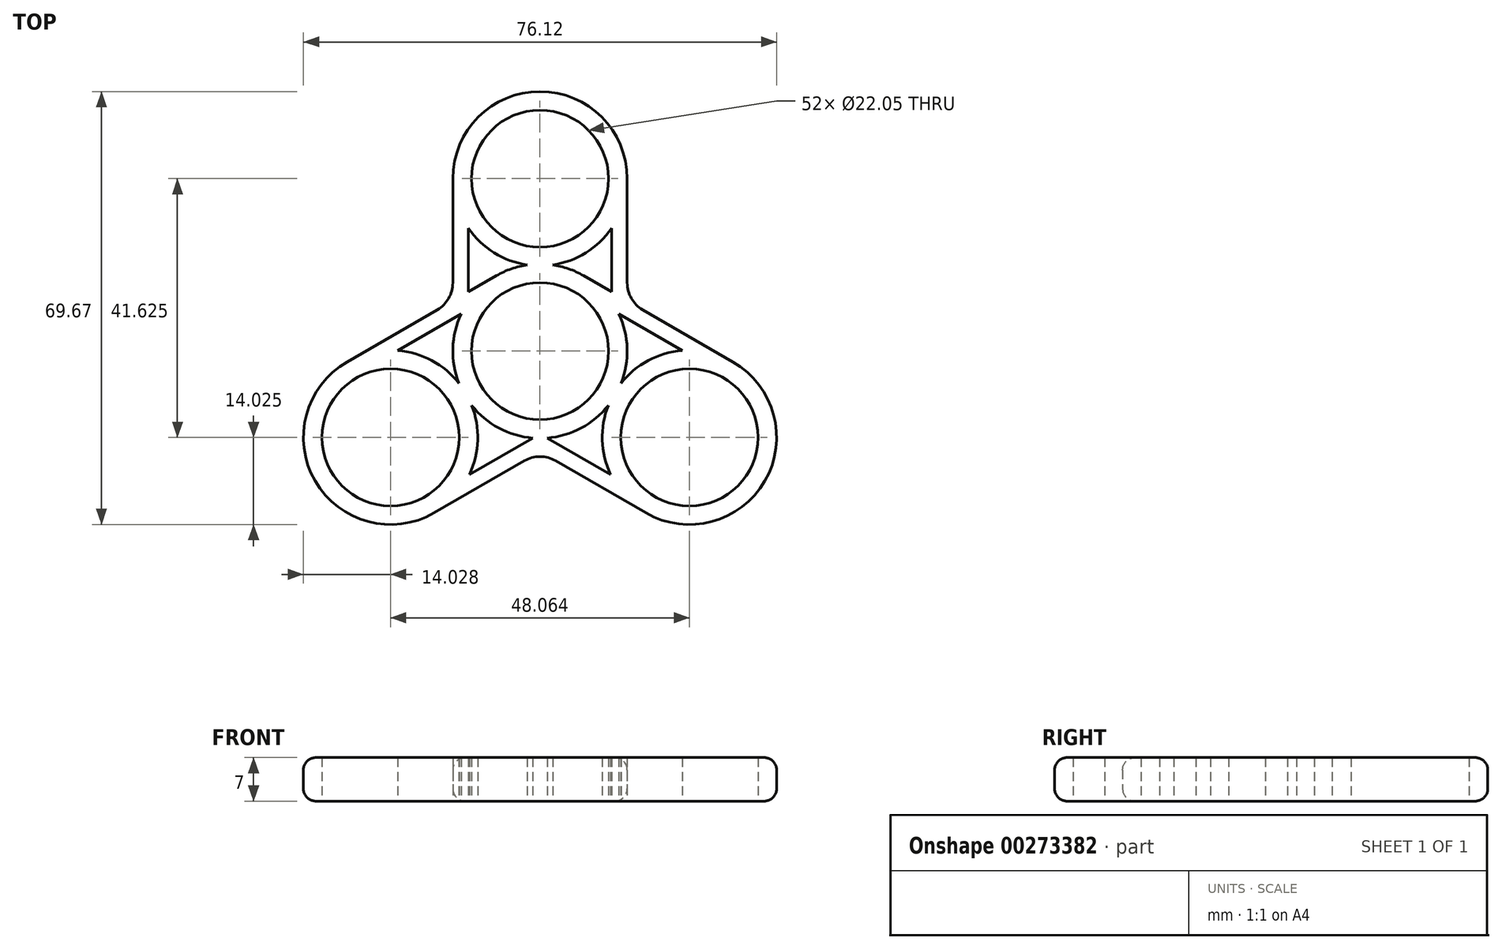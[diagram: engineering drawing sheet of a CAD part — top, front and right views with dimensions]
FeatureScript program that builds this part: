
annotation { "Feature Type Name" : "Feature", "Feature Type Description" : "" }
export const myFeature = defineFeature(function(context is Context, id is Id, definition is map)
    precondition{}
    {
        {
            var Q0;
            Q0=qCreatedBy(makeId("Top.planeOp"),FACE);
            var sketch = newSketch(context, id + "F0", { "sketchPlane" : qUnion([Q0])});
            skCircle(sketch, "E0", {"center": v(0, 0) * mm, "radius": 11.03 * mm});
            skCircle(sketch, "E1", {"center": v(0, 27.75) * mm, "radius": 11.03 * mm});
            skArc(sketch, "E2", {"start": v(2.05, 13.88) * mm, "mid": v(7.4, 15.83) * mm, "end": v(11.52, 19.76) * mm});
            skArc(sketch, "E3", {"start": v(-2.05, 13.88) * mm, "mid": v(-4.61, 13.25) * mm, "end": v(-7.01, 12.15) * mm});
            skLineSegment(sketch, "E4", {"start": v(-14.02, 27.75) * mm, "end": v(-14.02, 10.98) * mm});
            skLineSegment(sketch, "E5", {"start": v(-11.52, 9.54) * mm, "end": v(-11.52, 19.76) * mm});
            skArc(sketch, "E6.trimOffspring", {"start": v(-11.52, 19.76) * mm, "mid": v(-7.4, 15.83) * mm, "end": v(-2.05, 13.88) * mm});
            skLineSegment(sketch, "E7.MirrorCS", {"start": v(11.52, 9.54) * mm, "end": v(11.52, 19.76) * mm});
            skLineSegment(sketch, "E8.MirrorCS", {"start": v(14.02, 27.75) * mm, "end": v(14.02, 10.98) * mm});
            skArc(sketch, "E9.trimOffspring", {"start": v(14.02, 27.75) * mm, "mid": v(0, 41.77) * mm, "end": v(-14.02, 27.75) * mm});
            skArc(sketch, "E10.1.0", {"start": v(-11.35, -19.86) * mm, "mid": v(-10.01, -14.32) * mm, "end": v(-11, -8.7) * mm});
            skArc(sketch, "E10.1.1", {"start": v(-31.04, -1.73) * mm, "mid": v(-36.18, -20.89) * mm, "end": v(-17.02, -26.02) * mm});
            skArc(sketch, "E10.1.2", {"start": v(-13.04, -5.17) * mm, "mid": v(-17.4, -1.51) * mm, "end": v(-22.87, 0.1) * mm});
            skCircle(sketch, "E10.1.3", {"center": v(-24.03, -13.87) * mm, "radius": 11.03 * mm});
            skLineSegment(sketch, "E10.1.4", {"start": v(-12.68, 5.98) * mm, "end": v(-22.87, 0.1) * mm});
            skLineSegment(sketch, "E10.1.5", {"start": v(-31.04, -1.73) * mm, "end": v(-16.52, 6.65) * mm});
            skLineSegment(sketch, "E10.1.6", {"start": v(-1.16, -13.98) * mm, "end": v(-11.35, -19.86) * mm});
            skLineSegment(sketch, "E10.1.7", {"start": v(-17.02, -26.02) * mm, "end": v(-2.5, -17.64) * mm});
            skArc(sketch, "E10.2.0", {"start": v(22.87, 0.1) * mm, "mid": v(17.4, -1.51) * mm, "end": v(13.04, -5.17) * mm});
            skArc(sketch, "E10.2.1", {"start": v(17.02, -26.02) * mm, "mid": v(36.18, -20.89) * mm, "end": v(31.04, -1.73) * mm});
            skArc(sketch, "E10.2.2", {"start": v(11, -8.7) * mm, "mid": v(10.01, -14.32) * mm, "end": v(11.35, -19.86) * mm});
            skCircle(sketch, "E10.2.3", {"center": v(24.03, -13.88) * mm, "radius": 11.03 * mm});
            skLineSegment(sketch, "E10.2.4", {"start": v(1.16, -13.98) * mm, "end": v(11.35, -19.86) * mm});
            skLineSegment(sketch, "E10.2.5", {"start": v(17.02, -26.02) * mm, "end": v(2.5, -17.64) * mm});
            skLineSegment(sketch, "E10.2.6", {"start": v(12.68, 5.98) * mm, "end": v(22.87, 0.1) * mm});
            skLineSegment(sketch, "E10.2.7", {"start": v(31.04, -1.73) * mm, "end": v(16.52, 6.65) * mm});
            skLineSegment(sketch, "E11.trimOffspring", {"start": v(11.52, 9.54) * mm, "end": v(7.01, 12.15) * mm});
            skPoint(sketch, "E12.trimOffspring.end.orphan", {"position": v(14.02, 0) * mm});
            skPoint(sketch, "E13.orphan", {"position": v(11.52, 8) * mm});
            skArc(sketch, "E14.trimOffspring", {"start": v(7.01, 12.15) * mm, "mid": v(4.61, 13.25) * mm, "end": v(2.05, 13.88) * mm});
            skArc(sketch, "E15.trimOffspring", {"start": v(13.04, -5.17) * mm, "mid": v(14.02, 0.45) * mm, "end": v(12.68, 5.98) * mm});
            skArc(sketch, "E16.trimOffspring", {"start": v(-11, -8.7) * mm, "mid": v(-6.62, -12.36) * mm, "end": v(-1.16, -13.98) * mm});
            skArc(sketch, "E17.trimOffspring", {"start": v(-12.68, 5.98) * mm, "mid": v(-14.02, 0.45) * mm, "end": v(-13.04, -5.17) * mm});
            skLineSegment(sketch, "E18.trimOffspring", {"start": v(-11.52, 9.54) * mm, "end": v(-7.01, 12.15) * mm});
            skPoint(sketch, "E19.orphan", {"position": v(-11.52, 8) * mm});
            skPoint(sketch, "E20.trimOffspring.end.orphan", {"position": v(-14.02, 0) * mm});
            skPoint(sketch, "E21.orphan", {"position": v(-7.01, -12.15) * mm});
            skPoint(sketch, "E22.orphan", {"position": v(7.01, -12.15) * mm});
            skArc(sketch, "E23.trimOffspring", {"start": v(1.16, -13.98) * mm, "mid": v(6.62, -12.36) * mm, "end": v(11, -8.7) * mm});
            skPoint(sketch, "E24.visualSharp", {"position": v(-14.02, 8.1) * mm});
            skArc(sketch, "E24.filletArc", {"start": v(-16.53, 6.65) * mm, "mid": v(-14.7, 8.48) * mm, "end": v(-14.02, 10.98) * mm});
            skPoint(sketch, "E25.visualSharp", {"position": v(14.02, 8.1) * mm});
            skArc(sketch, "E25.filletArc", {"start": v(14.03, 10.98) * mm, "mid": v(14.7, 8.48) * mm, "end": v(16.52, 6.65) * mm});
            skPoint(sketch, "E26.visualSharp", {"position": v(0, -16.2) * mm});
            skArc(sketch, "E26.filletArc", {"start": v(2.5, -17.64) * mm, "mid": v(0, -16.97) * mm, "end": v(-2.5, -17.64) * mm});
            skLineSegment(sketch, "E27", {"start": v(-24.03, -27.9) * mm, "end": v(24.03, -27.9) * mm, "construction": true});
            skCircle(sketch, "E28", {"center": v(0, 0) * mm, "radius": 41.77 * mm, "construction": true});
            skSolve(sketch);
        }
        {
            var Q0;
            Q0=makeQuery(id+"F0.imprint","IMPRINT",FACE,{"disambiguationData":[TD([[makeQuery(id+"F0.imprint","IMPRINT",EDGE,{"derivedFrom":sQuery(id+"F0.wireOp",EDGE,"E0")}),-1.0]])]});
            extrude(context, id + "F1", {"entities" : qUnion([Q0]), "depth" : 7 * mm});
        }
        {
            var Q0;
            Q0=makeQuery(id+"F1.opExtrude","CAP_EDGE",EDGE,{"disambiguationData":[OSD([sQuery(id+"F0.wireOp",EDGE,"E10.1.1")])],"isStart":false});
            var Q1;
            Q1=makeQuery(id+"F1.opExtrude","CAP_EDGE",EDGE,{"disambiguationData":[OSD([sQuery(id+"F0.wireOp",EDGE,"E10.1.7")])],"isStart":false});
            var Q2;
            Q2=makeQuery(id+"F1.opExtrude","CAP_EDGE",EDGE,{"disambiguationData":[OSD([sQuery(id+"F0.wireOp",EDGE,"E26.filletArc")])],"isStart":false});
            var Q3;
            Q3=makeQuery(id+"F1.opExtrude","CAP_EDGE",EDGE,{"disambiguationData":[OSD([sQuery(id+"F0.wireOp",EDGE,"E10.2.5")])],"isStart":false});
            var Q4;
            Q4=makeQuery(id+"F1.opExtrude","CAP_EDGE",EDGE,{"disambiguationData":[OSD([sQuery(id+"F0.wireOp",EDGE,"E10.2.1")])],"isStart":false});
            var Q5;
            Q5=makeQuery(id+"F1.opExtrude","CAP_EDGE",EDGE,{"disambiguationData":[OSD([sQuery(id+"F0.wireOp",EDGE,"E10.2.7")])],"isStart":false});
            var Q6;
            Q6=makeQuery(id+"F1.opExtrude","CAP_EDGE",EDGE,{"disambiguationData":[OSD([sQuery(id+"F0.wireOp",EDGE,"E25.filletArc")])],"isStart":false});
            var Q7;
            Q7=makeQuery(id+"F1.opExtrude","CAP_EDGE",EDGE,{"disambiguationData":[OSD([sQuery(id+"F0.wireOp",EDGE,"E10.1.5")])],"isStart":false});
            var Q8;
            Q8=makeQuery(id+"F1.opExtrude","CAP_EDGE",EDGE,{"disambiguationData":[OSD([sQuery(id+"F0.wireOp",EDGE,"E24.filletArc")])],"isStart":false});
            var Q9;
            Q9=makeQuery(id+"F1.opExtrude","CAP_EDGE",EDGE,{"disambiguationData":[OSD([sQuery(id+"F0.wireOp",EDGE,"E9.trimOffspring")])],"isStart":false});
            var Q10;
            Q10=makeQuery(id+"F1.opExtrude","CAP_EDGE",EDGE,{"disambiguationData":[OSD([sQuery(id+"F0.wireOp",EDGE,"E8.MirrorCS")])],"isStart":false});
            var Q11;
            Q11=makeQuery(id+"F1.opExtrude","CAP_EDGE",EDGE,{"disambiguationData":[OSD([sQuery(id+"F0.wireOp",EDGE,"E10.1.5")])],"isStart":true});
            var Q12;
            Q12=makeQuery(id+"F1.opExtrude","CAP_EDGE",EDGE,{"disambiguationData":[OSD([sQuery(id+"F0.wireOp",EDGE,"E10.1.1")])],"isStart":true});
            fillet(context, id + "F2", {"entities" : qUnion([Q0, Q1, Q2, Q3, Q4, Q5, Q6, Q7, Q8, Q9, Q10, Q11, Q12]), "radius" : 2 * mm, "tangentPropagation" : true, "allowEdgeOverflow" : false});
        }
    });
